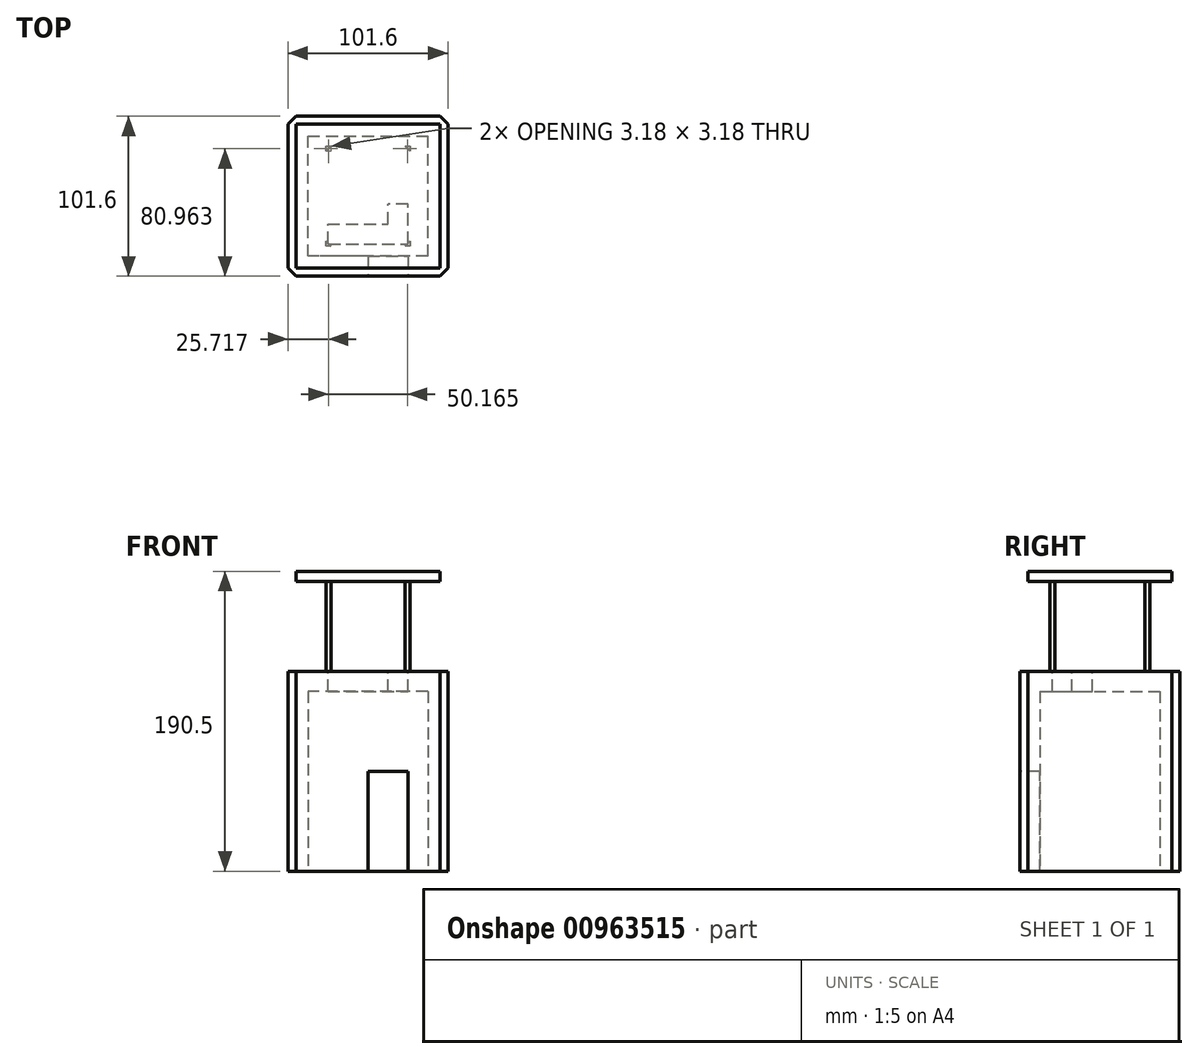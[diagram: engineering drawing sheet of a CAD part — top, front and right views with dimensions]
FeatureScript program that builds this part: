
annotation { "Feature Type Name" : "Feature", "Feature Type Description" : "" }
export const myFeature = defineFeature(function(context is Context, id is Id, definition is map)
    precondition{}
    {
        {
            var Q0;
            Q0=qCreatedBy(makeId("Top.planeOp"),FACE);
            var sketch = newSketch(context, id + "F0", { "sketchPlane" : qUnion([Q0])});
            skLineSegment(sketch, "E0.bottom", {"start": v(50.8, 50.8) * mm, "end": v(-50.8, 50.8) * mm});
            skLineSegment(sketch, "E0.top", {"start": v(50.8, -50.8) * mm, "end": v(-50.8, -50.8) * mm});
            skLineSegment(sketch, "E0.left", {"start": v(50.8, 50.8) * mm, "end": v(50.8, -50.8) * mm});
            skLineSegment(sketch, "E0.right", {"start": v(-50.8, 50.8) * mm, "end": v(-50.8, -50.8) * mm});
            skPoint(sketch, "E0.middle", {"position": v(0, 0) * mm});
            skLineSegment(sketch, "E1.0", {"start": v(38.1, 38.1) * mm, "end": v(-38.1, 38.1) * mm});
            skLineSegment(sketch, "E1.1", {"start": v(38.1, 38.1) * mm, "end": v(38.1, -38.1) * mm});
            skLineSegment(sketch, "E1.2", {"start": v(38.1, -38.1) * mm, "end": v(-38.1, -38.1) * mm});
            skLineSegment(sketch, "E1.3", {"start": v(-38.1, 38.1) * mm, "end": v(-38.1, -38.1) * mm});
            skSolve(sketch);
        }
        {
            var Q0;
            Q0=makeQuery(id+"F0.imprint","IMPRINT",FACE,{"disambiguationData":[TD([[makeQuery(id+"F0.imprint","IMPRINT",EDGE,{"derivedFrom":sQuery(id+"F0.wireOp",EDGE,"E0.bottom")}),1.0]])]});
            extrude(context, id + "F1", {"entities" : qUnion([Q0]), "depth" : 127 * mm, "offsetDistance" : 25.4 * mm});
        }
        {
            var Q0;
            Q0=makeQuery(id+"F1.opExtrude","SWEPT_FACE",FACE,{"disambiguationData":[OSD([sQuery(id+"F0.wireOp",EDGE,"E0.top")])]});
            var sketch = newSketch(context, id + "F2", { "sketchPlane" : qUnion([Q0])});
            skLineSegment(sketch, "E2.bottom", {"start": v(0, 0) * mm, "end": v(25.4, 0) * mm});
            skLineSegment(sketch, "E2.top", {"start": v(0, 63.5) * mm, "end": v(25.4, 63.5) * mm});
            skLineSegment(sketch, "E2.left", {"start": v(0, 0) * mm, "end": v(0, 63.5) * mm});
            skLineSegment(sketch, "E2.right", {"start": v(25.4, 0) * mm, "end": v(25.4, 63.5) * mm});
            skSolve(sketch);
        }
        {
            var Q0;
            Q0=makeQuery(id+"F2.imprint","IMPRINT",FACE,{"disambiguationData":[TD([[makeQuery(id+"F2.imprint","IMPRINT",EDGE,{"derivedFrom":sQuery(id+"F2.wireOp",EDGE,"E2.bottom")}),-1.0]])]});
            extrude(context, id + "F3", {"entities" : qUnion([Q0]), "operationType" : NewBodyOperationType.REMOVE, "oppositeDirection" : true, "depth" : 25.4 * mm, "offsetDistance" : 25.4 * mm});
        }
        {
            var Q0;
            Q0=makeQuery(id+"F1.opExtrude","SWEPT_FACE",FACE,{"disambiguationData":[OSD([sQuery(id+"F0.wireOp",EDGE,"E1.0")])]});
            var sketch = newSketch(context, id + "F4", { "sketchPlane" : qUnion([Q0])});
            skLineSegment(sketch, "E3.bottom", {"start": v(-38.1, 127) * mm, "end": v(38.1, 127) * mm});
            skLineSegment(sketch, "E3.top", {"start": v(-38.1, 114.3) * mm, "end": v(38.1, 114.3) * mm});
            skLineSegment(sketch, "E3.left", {"start": v(-38.1, 127) * mm, "end": v(-38.1, 114.3) * mm});
            skLineSegment(sketch, "E3.right", {"start": v(38.1, 127) * mm, "end": v(38.1, 114.3) * mm});
            skSolve(sketch);
        }
        {
            var Q0;
            Q0 = qSketchRegion(id + "F4", true);
            extrude(context, id + "F5", {"entities" : qUnion([Q0]), "operationType" : NewBodyOperationType.ADD, "depth" : 77.72 * mm, "offsetDistance" : 25.4 * mm});
        }
        {
            var Q0;
            Q0=makeQuery(id+"F5.boolean.opBoolean","MERGE",FACE,{"derivedFrom":[makeQuery(id+"F1.opExtrude","CAP_FACE",FACE,{"disambiguationData":[OSD([sQuery(id+"F0.wireOp",EDGE,"E0.bottom"),sQuery(id+"F0.wireOp",EDGE,"E0.top"),sQuery(id+"F0.wireOp",EDGE,"E0.left"),sQuery(id+"F0.wireOp",EDGE,"E0.right"),sQuery(id+"F0.wireOp",EDGE,"E1.0"),sQuery(id+"F0.wireOp",EDGE,"E1.1"),sQuery(id+"F0.wireOp",EDGE,"E1.2"),sQuery(id+"F0.wireOp",EDGE,"E1.3")])],"isStart":false}),makeQuery(id+"F5.opExtrude","SWEPT_FACE",FACE,{"disambiguationData":[OSD([sQuery(id+"F4.wireOp",EDGE,"E3.bottom")])]})]});
            var sketch = newSketch(context, id + "F6", { "sketchPlane" : qUnion([Q0])});
            skLineSegment(sketch, "E4.bottom", {"start": v(-25.4, -30.3) * mm, "end": v(25.4, -30.3) * mm});
            skLineSegment(sketch, "E4.top", {"start": v(-25.4, -17.6) * mm, "end": v(12.7, -17.6) * mm});
            skLineSegment(sketch, "E4.left", {"start": v(-25.4, -30.3) * mm, "end": v(-25.4, -17.6) * mm});
            skLineSegment(sketch, "E4.right", {"start": v(25.4, -30.3) * mm, "end": v(25.4, -17.6) * mm});
            skLineSegment(sketch, "E5.top", {"start": v(25.4, -4.9) * mm, "end": v(12.7, -4.9) * mm});
            skLineSegment(sketch, "E5.left", {"start": v(25.4, -17.6) * mm, "end": v(25.4, -4.9) * mm});
            skLineSegment(sketch, "E5.right", {"start": v(12.7, -17.6) * mm, "end": v(12.7, -4.9) * mm});
            skSolve(sketch);
        }
        {
            var Q0;
            Q0=makeQuery(id+"F6.imprint","IMPRINT",FACE,{"disambiguationData":[TD([[makeQuery(id+"F6.imprint","IMPRINT",EDGE,{"derivedFrom":sQuery(id+"F6.wireOp",EDGE,"E4.bottom")}),1.0]])]});
            extrude(context, id + "F7", {"entities" : qUnion([Q0]), "operationType" : NewBodyOperationType.REMOVE, "oppositeDirection" : true, "depth" : 25.4 * mm, "offsetDistance" : 25.4 * mm});
        }
        {
            var Q0;
            Q0=makeQuery(id+"F5.boolean.opBoolean","MERGE",FACE,{"derivedFrom":[makeQuery(id+"F1.opExtrude","CAP_FACE",FACE,{"disambiguationData":[OSD([sQuery(id+"F0.wireOp",EDGE,"E0.bottom"),sQuery(id+"F0.wireOp",EDGE,"E0.top"),sQuery(id+"F0.wireOp",EDGE,"E0.left"),sQuery(id+"F0.wireOp",EDGE,"E0.right"),sQuery(id+"F0.wireOp",EDGE,"E1.0"),sQuery(id+"F0.wireOp",EDGE,"E1.1"),sQuery(id+"F0.wireOp",EDGE,"E1.2"),sQuery(id+"F0.wireOp",EDGE,"E1.3")])],"isStart":false}),makeQuery(id+"F5.opExtrude","SWEPT_FACE",FACE,{"disambiguationData":[OSD([sQuery(id+"F4.wireOp",EDGE,"E3.bottom")])]})]});
            var sketch = newSketch(context, id + "F8", { "sketchPlane" : qUnion([Q0])});
            skLineSegment(sketch, "E6", {"start": v(-26.67, -28.57) * mm, "end": v(-23.5, -31.75) * mm});
            skLineSegment(sketch, "E7", {"start": v(-23.5, -31.75) * mm, "end": v(-26.67, -31.75) * mm});
            skLineSegment(sketch, "E8", {"start": v(-26.67, -31.75) * mm, "end": v(-26.67, -28.57) * mm});
            skPoint(sketch, "E9.center", {"position": v(0, 0) * mm});
            skLineSegment(sketch, "E10.0.1.0", {"start": v(-23.5, 31.75) * mm, "end": v(-26.67, 28.57) * mm});
            skLineSegment(sketch, "E10.0.1.1", {"start": v(-26.67, 31.75) * mm, "end": v(-23.5, 31.75) * mm});
            skLineSegment(sketch, "E10.0.1.2", {"start": v(-26.67, 28.57) * mm, "end": v(-26.67, 31.75) * mm});
            skLineSegment(sketch, "E10.1.0.0", {"start": v(23.5, -31.75) * mm, "end": v(26.67, -28.58) * mm});
            skLineSegment(sketch, "E10.1.0.1", {"start": v(26.67, -31.75) * mm, "end": v(23.5, -31.75) * mm});
            skLineSegment(sketch, "E10.1.0.2", {"start": v(26.67, -28.58) * mm, "end": v(26.67, -31.75) * mm});
            skLineSegment(sketch, "E10.1.1.0", {"start": v(26.67, 28.57) * mm, "end": v(23.5, 31.75) * mm});
            skLineSegment(sketch, "E10.1.1.1", {"start": v(26.67, 31.75) * mm, "end": v(26.67, 28.57) * mm});
            skLineSegment(sketch, "E10.1.1.2", {"start": v(23.5, 31.75) * mm, "end": v(26.67, 31.75) * mm});
            skSolve(sketch);
        }
        {
            var Q0;
            Q0 = qSketchRegion(id + "F8", true);
            extrude(context, id + "F9", {"entities" : qUnion([Q0]), "operationType" : NewBodyOperationType.ADD, "depth" : 57.15 * mm, "offsetDistance" : 25.4 * mm});
        }
        {
            var Q0;
            Q0=makeQuery(id+"F9.opExtrude","CAP_FACE",FACE,{"disambiguationData":[OSD([sQuery(id+"F8.wireOp",EDGE,"E10.0.1.0"),sQuery(id+"F8.wireOp",EDGE,"E10.0.1.1"),sQuery(id+"F8.wireOp",EDGE,"E10.0.1.2")])],"isStart":false});
            var sketch = newSketch(context, id + "F10", { "sketchPlane" : qUnion([Q0])});
            skLineSegment(sketch, "E11.bottom", {"start": v(-45.72, 45.72) * mm, "end": v(45.72, 45.72) * mm});
            skLineSegment(sketch, "E11.top", {"start": v(-45.72, -45.72) * mm, "end": v(45.72, -45.72) * mm});
            skLineSegment(sketch, "E11.left", {"start": v(-45.72, 45.72) * mm, "end": v(-45.72, -45.72) * mm});
            skLineSegment(sketch, "E11.right", {"start": v(45.72, 45.72) * mm, "end": v(45.72, -45.72) * mm});
            skSolve(sketch);
        }
        {
            var Q0;
            Q0 = qSketchRegion(id + "F10", true);
            extrude(context, id + "F11", {"entities" : qUnion([Q0]), "operationType" : NewBodyOperationType.ADD, "depth" : 6.35 * mm, "offsetDistance" : 25.4 * mm});
        }
        {
            var Q0;
            Q0=makeQuery(id+"F1.opExtrude","SWEPT_EDGE",EDGE,{"disambiguationData":[OSD([sQuery(id+"F0.wireOp",EDGE,"E0.top"),sQuery(id+"F0.wireOp",EDGE,"E0.left")])]});
            var Q1;
            Q1=makeQuery(id+"F1.opExtrude","SWEPT_EDGE",EDGE,{"disambiguationData":[OSD([sQuery(id+"F0.wireOp",EDGE,"E0.top"),sQuery(id+"F0.wireOp",EDGE,"E0.right")])]});
            var Q2;
            Q2=makeQuery(id+"F1.opExtrude","SWEPT_EDGE",EDGE,{"disambiguationData":[OSD([sQuery(id+"F0.wireOp",EDGE,"E0.bottom"),sQuery(id+"F0.wireOp",EDGE,"E0.left")])]});
            var Q3;
            Q3=makeQuery(id+"F1.opExtrude","SWEPT_EDGE",EDGE,{"disambiguationData":[OSD([sQuery(id+"F0.wireOp",EDGE,"E0.bottom"),sQuery(id+"F0.wireOp",EDGE,"E0.right")])]});
            chamfer(context, id + "F12", {"entities" : qUnion([Q0, Q1, Q2, Q3]), "chamferType" : ChamferType.OFFSET_ANGLE, "width" : 5.08 * mm, "oppositeDirection" : false, "angle" : 45 * degree, "tangentPropagation" : true});
        }
    });
